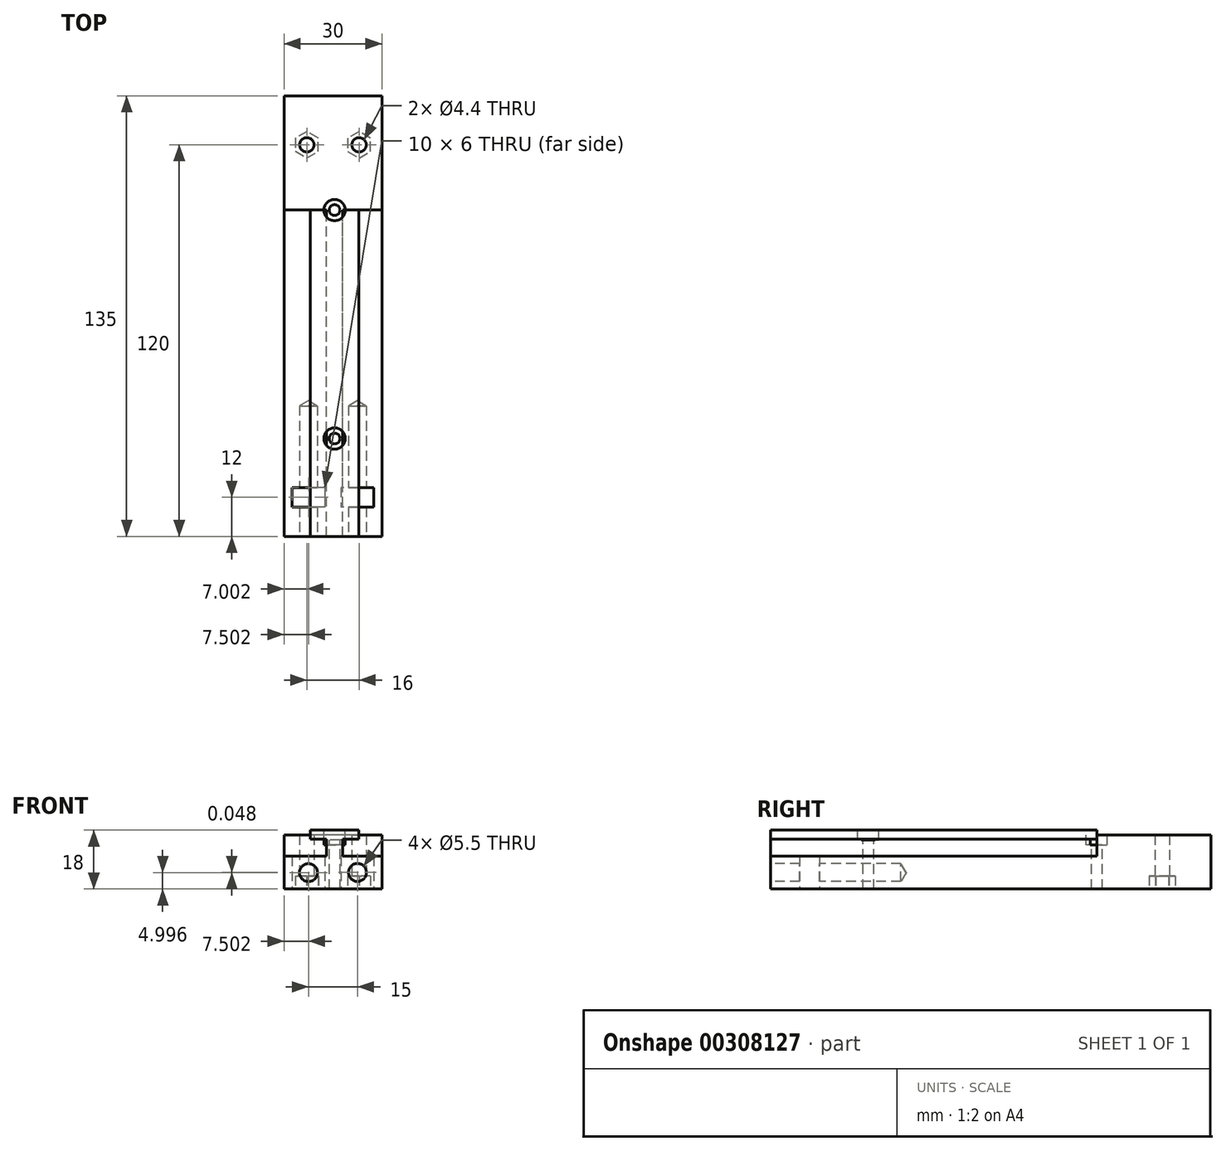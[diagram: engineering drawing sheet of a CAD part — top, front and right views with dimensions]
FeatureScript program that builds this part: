
annotation { "Feature Type Name" : "Feature", "Feature Type Description" : "" }
export const myFeature = defineFeature(function(context is Context, id is Id, definition is map)
    precondition{}
    {
        {
            var Q0;
            Q0=qCreatedBy(makeId("Front.planeOp"),FACE);
            var sketch = newSketch(context, id + "F0", { "sketchPlane" : qUnion([Q0])});
            skPoint(sketch, "E0.0", {"position": v(-38.5, -5.75) * mm});
            skPoint(sketch, "E1.0", {"position": v(-8.5, 4.25) * mm});
            skPoint(sketch, "E2.0", {"position": v(-20.51, 4.25) * mm});
            skPoint(sketch, "E3.0", {"position": v(-25.51, 9.45) * mm});
            skPoint(sketch, "E4.0", {"position": v(-33.16, 0.5) * mm});
            skPoint(sketch, "E5.0", {"position": v(-32.25, -2.92) * mm});
            skPoint(sketch, "E6.0", {"position": v(-28.5, -0.75) * mm});
            skPoint(sketch, "E7.0", {"position": v(-18.16, -1.96) * mm});
            skPoint(sketch, "E8.0", {"position": v(-14.23, 1.06) * mm});
            skPoint(sketch, "E9.0", {"position": v(-13.83, -1.96) * mm});
            skCircle(sketch, "E10", {"center": v(-31, -0.75) * mm, "radius": 2.5 * mm});
            skCircle(sketch, "E11", {"center": v(-16, -0.7) * mm, "radius": 2.5 * mm});
            skLineSegment(sketch, "E12.bottom", {"start": v(-38.5, -5.75) * mm, "end": v(-38.5, 4.25) * mm});
            skLineSegment(sketch, "E12.top", {"start": v(-8.5, -5.75) * mm, "end": v(-8.5, 4.25) * mm});
            skLineSegment(sketch, "E12.left", {"start": v(-38.5, -5.75) * mm, "end": v(-8.5, -5.75) * mm});
            skLineSegment(sketch, "E12.right", {"start": v(-38.5, 4.25) * mm, "end": v(-8.5, 4.25) * mm});
            skLineSegment(sketch, "E13.bottom", {"start": v(-25.51, 9.45) * mm, "end": v(-25.51, 4.25) * mm});
            skLineSegment(sketch, "E13.top", {"start": v(-20.51, 9.45) * mm, "end": v(-20.51, 4.25) * mm});
            skLineSegment(sketch, "E13.left", {"start": v(-25.51, 9.45) * mm, "end": v(-20.51, 9.45) * mm});
            skLineSegment(sketch, "E13.right", {"start": v(-25.51, 4.25) * mm, "end": v(-20.51, 4.25) * mm});
            skLineSegment(sketch, "E14", {"start": v(-20.51, 9.45) * mm, "end": v(-15.61, 9.45) * mm});
            skLineSegment(sketch, "E15", {"start": v(-15.61, 9.45) * mm, "end": v(-15.61, 12.25) * mm});
            skLineSegment(sketch, "E16", {"start": v(-15.61, 12.25) * mm, "end": v(-30.41, 12.25) * mm});
            skLineSegment(sketch, "E17", {"start": v(-30.41, 12.25) * mm, "end": v(-30.41, 9.45) * mm});
            skLineSegment(sketch, "E18", {"start": v(-30.41, 9.45) * mm, "end": v(-25.51, 9.45) * mm});
            skLineSegment(sketch, "E19", {"start": v(-30.41, 9.45) * mm, "end": v(-30.41, 4.25) * mm});
            skLineSegment(sketch, "E20", {"start": v(-15.61, 9.45) * mm, "end": v(-15.61, 4.25) * mm});
            skSolve(sketch);
        }
        {
            var Q0;
            Q0=makeQuery(id+"F0.imprint","IMPRINT",FACE,{"disambiguationData":[TD([[makeQuery(id+"F0.imprint","IMPRINT",EDGE,{"derivedFrom":sQuery(id+"F0.wireOp",EDGE,"E10")}),-1.0]])]});
            var Q1;
            {var subQ0=sQuery(id+"F0.wireOp",EDGE,"E13.bottom");Q1=makeQuery(id+"F0.imprint","IMPRINT",FACE,{"disambiguationData":[TD([[makeQuery(id+"F0.imprint","IMPRINT",EDGE,{"derivedFrom":subQ0}),1.0]])]});}
            var Q2;
            {var subQ2=sQuery(id+"F0.wireOp",EDGE,"ff0e58af-8eab-48c5-9db7-a835ad51614d.bottom");Q2=makeQuery(id+"F0.imprint","IMPRINT",FACE,{"disambiguationData":[TD([[makeQuery(id+"F0.imprint","IMPRINT",EDGE,{"derivedFrom":subQ2}),1.0]])]});}
            var Q3;
            Q3=makeQuery(id+"F0.imprint","IMPRINT",FACE,{"disambiguationData":[TD([[makeQuery(id+"F0.imprint","IMPRINT",EDGE,{"derivedFrom":sQuery(id+"F0.wireOp",EDGE,"E10")}),1.0]])]});
            var Q4;
            Q4=makeQuery(id+"F0.imprint","IMPRINT",FACE,{"disambiguationData":[TD([[makeQuery(id+"F0.imprint","IMPRINT",EDGE,{"derivedFrom":sQuery(id+"F0.wireOp",EDGE,"E11")}),1.0]])]});
            var Q5;
            Q5=makeQuery(id+"F0.imprint","IMPRINT",FACE,{"disambiguationData":[TD([[makeQuery(id+"F0.imprint","IMPRINT",EDGE,{"derivedFrom":sQuery(id+"F0.wireOp",EDGE,"E13.left")}),1.0]])]});
            extrude(context, id + "F1", {"entities" : qUnion([Q0, Q1, Q2, Q3, Q4, Q5]), "depth" : 100 * mm});
        }
        {
            var Q0;
            Q0=makeQuery(id+"F1.opExtrude","CAP_FACE",FACE,{"disambiguationData":[OSD([sQuery(id+"F0.wireOp",EDGE,"E10"),sQuery(id+"F0.wireOp",EDGE,"E11"),sQuery(id+"F0.wireOp",EDGE,"E12.bottom"),sQuery(id+"F0.wireOp",EDGE,"E12.top"),sQuery(id+"F0.wireOp",EDGE,"E12.left"),sQuery(id+"F0.wireOp",EDGE,"E12.right"),sQuery(id+"F0.wireOp",EDGE,"E13.bottom"),sQuery(id+"F0.wireOp",EDGE,"E13.top"),sQuery(id+"F0.wireOp",EDGE,"ff0e58af-8eab-48c5-9db7-a835ad51614d.bottom"),sQuery(id+"F0.wireOp",EDGE,"ff0e58af-8eab-48c5-9db7-a835ad51614d.top"),sQuery(id+"F0.wireOp",EDGE,"ff0e58af-8eab-48c5-9db7-a835ad51614d.left"),sQuery(id+"F0.wireOp",EDGE,"ff0e58af-8eab-48c5-9db7-a835ad51614d.right")])],"isStart":true});
            var sketch = newSketch(context, id + "F2", { "sketchPlane" : qUnion([Q0])});
            skLineSegment(sketch, "E21.bottom", {"start": v(8.5, -5.75) * mm, "end": v(38.5, -5.75) * mm});
            skLineSegment(sketch, "E21.top", {"start": v(8.5, 10.75) * mm, "end": v(38.5, 10.75) * mm});
            skLineSegment(sketch, "E21.left", {"start": v(8.5, -5.75) * mm, "end": v(8.5, 10.75) * mm});
            skLineSegment(sketch, "E21.right", {"start": v(38.5, -5.75) * mm, "end": v(38.5, 10.75) * mm});
            skSolve(sketch);
        }
        {
            var Q0;
            {var subQ0=sQuery(id+"F0.wireOp",EDGE,"E13.top");Q0=makeQuery(id+"F2.imprint","IMPRINT",FACE,{"disambiguationData":[TD([[makeQuery(id+"F2.imprint","IMPRINT",EDGE,{"derivedFrom":makeQuery(id+"F1.opExtrude","CAP_EDGE",EDGE,{"disambiguationData":[OSD([subQ0])],"isStart":true})}),-1.0]])]});}
            var Q1;
            {var subQ1=sQuery(id+"F0.wireOp",EDGE,"E13.bottom");Q1=makeQuery(id+"F2.imprint","IMPRINT",FACE,{"disambiguationData":[TD([[makeQuery(id+"F2.imprint","IMPRINT",EDGE,{"derivedFrom":makeQuery(id+"F1.opExtrude","CAP_EDGE",EDGE,{"disambiguationData":[OSD([subQ1])],"isStart":true})}),1.0]])]});}
            var Q2;
            Q2=makeQuery(id+"F2.imprint","IMPRINT",FACE,{"disambiguationData":[TD([[makeQuery(id+"F2.imprint","IMPRINT",EDGE,{"derivedFrom":makeQuery(id+"F1.opExtrude","CAP_EDGE",EDGE,{"disambiguationData":[OSD([sQuery(id+"F0.wireOp",EDGE,"E10")])],"isStart":true})}),-1.0]])]});
            var Q3;
            Q3=makeQuery(id+"F2.imprint","IMPRINT",FACE,{"disambiguationData":[TD([[makeQuery(id+"F2.imprint","IMPRINT",EDGE,{"derivedFrom":makeQuery(id+"F1.opExtrude","CAP_EDGE",EDGE,{"disambiguationData":[OSD([sQuery(id+"F0.wireOp",EDGE,"E11")])],"isStart":true})}),-1.0]])]});
            var Q4;
            {var subQ6=sQuery(id+"F2.wireOp",EDGE,"E21.bottom");Q4=makeQuery(id+"F2.imprint","IMPRINT",FACE,{"disambiguationData":[TD([[makeQuery(id+"F2.imprint","IMPRINT",EDGE,{"derivedFrom":subQ6}),-1.0]])]});}
            extrude(context, id + "F3", {"entities" : qUnion([Q0, Q1, Q2, Q3, Q4]), "depth" : 35 * mm});
        }
        {
            var Q0;
            Q0=makeQuery(id+"F3.opExtrude","SWEPT_BODY",BODY,{"disambiguationData":[OSD([sQuery(id+"F2.wireOp",EDGE,"E21.bottom"),sQuery(id+"F2.wireOp",EDGE,"E21.top"),sQuery(id+"F2.wireOp",EDGE,"E21.left"),sQuery(id+"F2.wireOp",EDGE,"E21.right")])]});
            var Q1;
            Q1=makeQuery(id+"F1.opExtrude","SWEPT_BODY",BODY,{"disambiguationData":[OSD([sQuery(id+"F0.wireOp",EDGE,"E10"),sQuery(id+"F0.wireOp",EDGE,"E11"),sQuery(id+"F0.wireOp",EDGE,"E12.bottom"),sQuery(id+"F0.wireOp",EDGE,"E12.top"),sQuery(id+"F0.wireOp",EDGE,"E12.left"),sQuery(id+"F0.wireOp",EDGE,"E12.right"),sQuery(id+"F0.wireOp",EDGE,"E13.bottom"),sQuery(id+"F0.wireOp",EDGE,"E13.top"),sQuery(id+"F0.wireOp",EDGE,"ff0e58af-8eab-48c5-9db7-a835ad51614d.bottom"),sQuery(id+"F0.wireOp",EDGE,"ff0e58af-8eab-48c5-9db7-a835ad51614d.top"),sQuery(id+"F0.wireOp",EDGE,"ff0e58af-8eab-48c5-9db7-a835ad51614d.left"),sQuery(id+"F0.wireOp",EDGE,"ff0e58af-8eab-48c5-9db7-a835ad51614d.right")])]});
            booleanBodies(context, id + "F4", {"operationType" : BooleanOperationType.UNION, "tools" : qUnion([Q0, Q1])});
        }
        {
            var Q0;
            Q0=makeQuery(id+"F4.opBoolean","MERGE",FACE,{"derivedFrom":[makeQuery(id+"F1.opExtrude","SWEPT_FACE",FACE,{"disambiguationData":[OSD([sQuery(id+"F0.wireOp",EDGE,"E12.left")])]}),makeQuery(id+"F3.opExtrude","SWEPT_FACE",FACE,{"disambiguationData":[OSD([sQuery(id+"F2.wireOp",EDGE,"E21.bottom")])]})]});
            var sketch = newSketch(context, id + "F5", { "sketchPlane" : qUnion([Q0])});
            skPoint(sketch, "E22", {"position": v(-15.5, -20) * mm});
            skPoint(sketch, "E23", {"position": v(-31.5, -20) * mm});
            skLineSegment(sketch, "E24.bottom", {"start": v(-11, 85) * mm, "end": v(-21, 85) * mm});
            skLineSegment(sketch, "E24.top", {"start": v(-11, 91) * mm, "end": v(-21, 91) * mm});
            skLineSegment(sketch, "E24.left", {"start": v(-11, 85) * mm, "end": v(-11, 91) * mm});
            skLineSegment(sketch, "E24.right", {"start": v(-21, 85) * mm, "end": v(-21, 91) * mm});
            skLineSegment(sketch, "E25.bottom", {"start": v(-26, 85) * mm, "end": v(-36, 85) * mm});
            skLineSegment(sketch, "E25.top", {"start": v(-26, 91) * mm, "end": v(-36, 91) * mm});
            skLineSegment(sketch, "E25.left", {"start": v(-26, 85) * mm, "end": v(-26, 91) * mm});
            skLineSegment(sketch, "E25.right", {"start": v(-36, 85) * mm, "end": v(-36, 91) * mm});
            skCircle(sketch, "E26.cCircle", {"center": v(-15.5, -20) * mm, "radius": 3.5 * mm, "construction": true});
            skLineSegment(sketch, "E26.0", {"start": v(-19, -22.02) * mm, "end": v(-19, -17.98) * mm});
            skLineSegment(sketch, "E26.1", {"start": v(-19, -17.98) * mm, "end": v(-15.5, -15.96) * mm});
            skLineSegment(sketch, "E26.2", {"start": v(-15.5, -15.96) * mm, "end": v(-12, -17.98) * mm});
            skLineSegment(sketch, "E26.3", {"start": v(-12, -17.98) * mm, "end": v(-12, -22.02) * mm});
            skLineSegment(sketch, "E26.4", {"start": v(-12, -22.02) * mm, "end": v(-15.5, -24.04) * mm});
            skLineSegment(sketch, "E26.5", {"start": v(-15.5, -24.04) * mm, "end": v(-19, -22.02) * mm});
            skPoint(sketch, "E26.0.midPoint", {"position": v(-19, -20) * mm});
            skCircle(sketch, "E27.cCircle", {"center": v(-31.5, -20) * mm, "radius": 3.5 * mm, "construction": true});
            skLineSegment(sketch, "E27.0", {"start": v(-27.96, -21.96) * mm, "end": v(-31.42, -24.04) * mm});
            skLineSegment(sketch, "E27.1", {"start": v(-31.42, -24.04) * mm, "end": v(-34.96, -22.08) * mm});
            skLineSegment(sketch, "E27.2", {"start": v(-34.96, -22.08) * mm, "end": v(-35.03, -18.04) * mm});
            skLineSegment(sketch, "E27.3", {"start": v(-35.03, -18.04) * mm, "end": v(-31.57, -15.96) * mm});
            skLineSegment(sketch, "E27.4", {"start": v(-31.57, -15.96) * mm, "end": v(-28.04, -17.92) * mm});
            skLineSegment(sketch, "E27.5", {"start": v(-28.04, -17.92) * mm, "end": v(-27.96, -21.96) * mm});
            skPoint(sketch, "E27.0.midPoint", {"position": v(-29.7, -23) * mm});
            skSolve(sketch);
        }
        {
            var Q0;
            Q0=sQuery(id+"F5.wireOp",VERTEX,"E22");
            var Q1;
            Q1=sQuery(id+"F5.wireOp",VERTEX,"E23");
            var Q2;
            Q2=makeQuery(id+"F3.opExtrude","SWEPT_BODY",BODY,{"disambiguationData":[OSD([sQuery(id+"F2.wireOp",EDGE,"E21.bottom"),sQuery(id+"F2.wireOp",EDGE,"E21.top"),sQuery(id+"F2.wireOp",EDGE,"E21.left"),sQuery(id+"F2.wireOp",EDGE,"E21.right")])]});
            hole(context, id + "F6", {"style" : HoleStyle.SIMPLE, "endStyle" : HoleEndStyle.BLIND, "standardTappedOrClearance" : lookupTablePath({ "standard" : "ISO", "fit" : "Normal", "size" : "M4", "type" : "Clearance" }), "standardBlindInLast" : lookupTablePath({ "fit" : "Standard", "standard" : "ISO", "size" : "M4", "type" : "Clearance" }), "holeDiameter" : 4.4 * mm, "holeDepth" : 40 * mm, "isTappedThrough" : true, "tappedDepth" : 12 * mm, "tapClearance" : 3, "locations" : qUnion([Q0, Q1]), "scope" : qUnion([Q2])});
        }
        {
            var Q0;
            Q0=makeQuery(id+"F5.imprint","IMPRINT",FACE,{"disambiguationData":[TD([[makeQuery(id+"F5.imprint","IMPRINT",EDGE,{"derivedFrom":sQuery(id+"F5.wireOp",EDGE,"E24.bottom")}),-1.0]])]});
            var Q1;
            Q1=makeQuery(id+"F5.imprint","IMPRINT",FACE,{"disambiguationData":[TD([[makeQuery(id+"F5.imprint","IMPRINT",EDGE,{"derivedFrom":sQuery(id+"F5.wireOp",EDGE,"E25.bottom")}),-1.0]])]});
            extrude(context, id + "F7", {"entities" : qUnion([Q0, Q1]), "operationType" : NewBodyOperationType.REMOVE, "oppositeDirection" : true, "depth" : 10 * mm});
        }
        {
            var Q0;
            Q0=makeQuery(id+"F1.opExtrude","CAP_FACE",FACE,{"disambiguationData":[OSD([sQuery(id+"F0.wireOp",EDGE,"E12.bottom"),sQuery(id+"F0.wireOp",EDGE,"E12.top"),sQuery(id+"F0.wireOp",EDGE,"E12.left"),sQuery(id+"F0.wireOp",EDGE,"E12.right"),sQuery(id+"F0.wireOp",EDGE,"E13.bottom"),sQuery(id+"F0.wireOp",EDGE,"E13.top"),sQuery(id+"F0.wireOp",EDGE,"ff0e58af-8eab-48c5-9db7-a835ad51614d.bottom"),sQuery(id+"F0.wireOp",EDGE,"ff0e58af-8eab-48c5-9db7-a835ad51614d.top"),sQuery(id+"F0.wireOp",EDGE,"ff0e58af-8eab-48c5-9db7-a835ad51614d.left"),sQuery(id+"F0.wireOp",EDGE,"ff0e58af-8eab-48c5-9db7-a835ad51614d.right")])],"isStart":false});
            var sketch = newSketch(context, id + "F8", { "sketchPlane" : qUnion([Q0])});
            skPoint(sketch, "E28.0", {"position": v(-31, -0.75) * mm});
            skPoint(sketch, "E29.0", {"position": v(-16, -0.7) * mm});
            skSolve(sketch);
        }
        {
            var Q0;
            Q0=sQuery(id+"F8.wireOp",VERTEX,"E28.0");
            var Q1;
            Q1=sQuery(id+"F8.wireOp",VERTEX,"E29.0");
            var Q2;
            Q2=makeQuery(id+"F3.opExtrude","SWEPT_BODY",BODY,{"disambiguationData":[OSD([sQuery(id+"F2.wireOp",EDGE,"E21.bottom"),sQuery(id+"F2.wireOp",EDGE,"E21.top"),sQuery(id+"F2.wireOp",EDGE,"E21.left"),sQuery(id+"F2.wireOp",EDGE,"E21.right")])]});
            hole(context, id + "F9", {"style" : HoleStyle.SIMPLE, "endStyle" : HoleEndStyle.BLIND, "standardTappedOrClearance" : lookupTablePath({ "standard" : "ISO", "fit" : "Normal", "size" : "M5", "type" : "Clearance" }), "standardBlindInLast" : lookupTablePath({ "fit" : "Standard", "standard" : "ISO", "size" : "M5", "type" : "Clearance" }), "holeDiameter" : 5.5 * mm, "holeDepth" : 40 * mm, "isTappedThrough" : true, "tappedDepth" : 12 * mm, "tapClearance" : 3, "locations" : qUnion([Q0, Q1]), "scope" : qUnion([Q2])});
        }
        {
            var Q0;
            Q0=makeQuery(id+"F1.opExtrude","SWEPT_FACE",FACE,{"disambiguationData":[OSD([sQuery(id+"F0.wireOp",EDGE,"E16")])]});
            var sketch = newSketch(context, id + "F10", { "sketchPlane" : qUnion([Q0])});
            skLineSegment(sketch, "E30", {"start": v(-23.01, -100) * mm, "end": v(-23.01, 0) * mm, "construction": true});
            skPoint(sketch, "E31", {"position": v(-23.01, -70) * mm});
            skPoint(sketch, "E32", {"position": v(-23.01, 0) * mm});
            skSolve(sketch);
        }
        {
            var Q0;
            Q0=sQuery(id+"F10.wireOp",VERTEX,"E30.end");
            var Q1;
            Q1=sQuery(id+"F10.wireOp",VERTEX,"E31");
            var Q2;
            Q2=makeQuery(id+"F3.opExtrude","SWEPT_BODY",BODY,{"disambiguationData":[OSD([sQuery(id+"F2.wireOp",EDGE,"E21.bottom"),sQuery(id+"F2.wireOp",EDGE,"E21.top"),sQuery(id+"F2.wireOp",EDGE,"E21.left"),sQuery(id+"F2.wireOp",EDGE,"E21.right")])]});
            hole(context, id + "F11", {"style" : HoleStyle.C_BORE, "endStyle" : HoleEndStyle.BLIND, "standardTappedOrClearance" : lookupTablePath({ "standard" : "ISO", "fit" : "Normal", "size" : "M3", "type" : "Clearance" }), "standardBlindInLast" : lookupTablePath({ "fit" : "Standard", "standard" : "ISO", "size" : "M3", "type" : "Clearance" }), "holeDiameter" : 3.3 * mm, "cBoreDiameter" : 6.5 * mm, "cBoreDepth" : 3 * mm, "holeDepth" : 20 * mm, "isTappedThrough" : true, "tappedDepth" : 12 * mm, "tapClearance" : 3, "locations" : qUnion([Q0, Q1]), "scope" : qUnion([Q2])});
        }
        {
            var Q0;
            Q0=makeQuery(id+"F5.imprint","IMPRINT",FACE,{"disambiguationData":[TD([[makeQuery(id+"F5.imprint","IMPRINT",EDGE,{"derivedFrom":sQuery(id+"F5.wireOp",EDGE,"E26.0")}),-1.0]])]});
            var Q1;
            Q1=makeQuery(id+"F5.imprint","IMPRINT",FACE,{"disambiguationData":[TD([[makeQuery(id+"F5.imprint","IMPRINT",EDGE,{"derivedFrom":sQuery(id+"F5.wireOp",EDGE,"E27.0")}),-1.0]])]});
            extrude(context, id + "F12", {"entities" : qUnion([Q0, Q1]), "operationType" : NewBodyOperationType.REMOVE, "oppositeDirection" : true, "depth" : 4 * mm});
        }
    });
